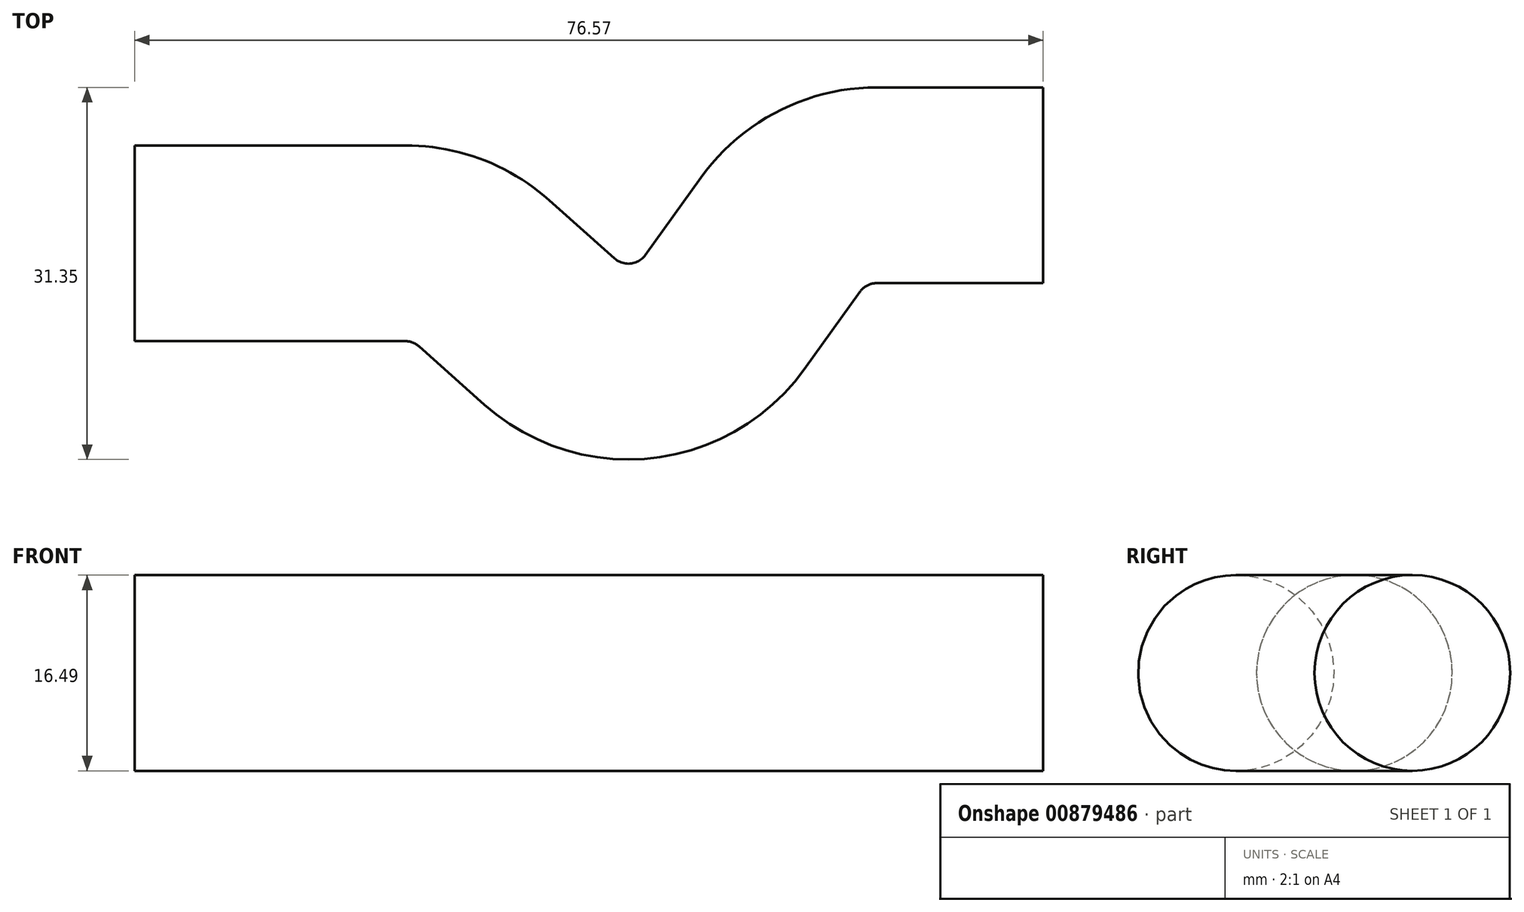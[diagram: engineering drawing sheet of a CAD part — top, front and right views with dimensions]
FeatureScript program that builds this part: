
annotation { "Feature Type Name" : "Feature", "Feature Type Description" : "" }
export const myFeature = defineFeature(function(context is Context, id is Id, definition is map)
    precondition{}
    {
        {
            var Q0;
            Q0=qCreatedBy(makeId("Top.planeOp"),FACE);
            var sketch = newSketch(context, id + "F0", { "sketchPlane" : qUnion([Q0])});
            skLineSegment(sketch, "E0", {"start": v(0, 0) * mm, "end": v(22.8, 0) * mm});
            skLineSegment(sketch, "E1", {"start": v(29.45, -2.53) * mm, "end": v(34.96, -7.44) * mm});
            skLineSegment(sketch, "E2", {"start": v(49.74, -5.8) * mm, "end": v(54.43, 0.72) * mm});
            skLineSegment(sketch, "E3", {"start": v(62.55, 4.89) * mm, "end": v(76.57, 4.89) * mm});
            skPoint(sketch, "E4.visualSharp", {"position": v(26.61, 0) * mm});
            skArc(sketch, "E4.filletArc", {"start": v(29.45, -2.53) * mm, "mid": v(26.36, -0.65) * mm, "end": v(22.8, 0) * mm});
            skPoint(sketch, "E5.visualSharp", {"position": v(43.26, -14.83) * mm});
            skArc(sketch, "E5.filletArc", {"start": v(34.96, -7.44) * mm, "mid": v(42.71, -9.91) * mm, "end": v(49.74, -5.8) * mm});
            skPoint(sketch, "E6.visualSharp", {"position": v(57.42, 4.89) * mm});
            skArc(sketch, "E6.filletArc", {"start": v(62.55, 4.89) * mm, "mid": v(57.98, 3.78) * mm, "end": v(54.43, 0.72) * mm});
            skSolve(sketch);
        }
        {
            var Q0;
            Q0=qCreatedBy(makeId("Right.planeOp"),FACE);
            var sketch = newSketch(context, id + "F1", { "sketchPlane" : qUnion([Q0])});
            skCircle(sketch, "E7", {"center": v(0, 0.63) * mm, "radius": 8.25 * mm});
            skSolve(sketch);
        }
        {
            var Q0;
            Q0=makeQuery(id+"F1.imprint","IMPRINT",FACE,{"disambiguationData":[TD([[makeQuery(id+"F1.imprint","IMPRINT",EDGE,{"derivedFrom":sQuery(id+"F1.wireOp",EDGE,"E7")}),1.0]])]});
            var Q1;
            Q1=sQuery(id+"F0.wireOp",EDGE,"E0");
            var Q2;
            Q2=sQuery(id+"F0.wireOp",EDGE,"E4.filletArc");
            var Q3;
            Q3=sQuery(id+"F0.wireOp",EDGE,"E1");
            var Q4;
            Q4=sQuery(id+"F0.wireOp",EDGE,"E5.filletArc");
            var Q5;
            Q5=sQuery(id+"F0.wireOp",EDGE,"E2");
            var Q6;
            Q6=sQuery(id+"F0.wireOp",EDGE,"E6.filletArc");
            var Q7;
            Q7=sQuery(id+"F0.wireOp",EDGE,"E3");
            sweep(context, id + "F2", {"profiles" : qUnion([Q0]), "path" : qUnion([Q1, Q2, Q3, Q4, Q5, Q6, Q7])});
        }
    });
